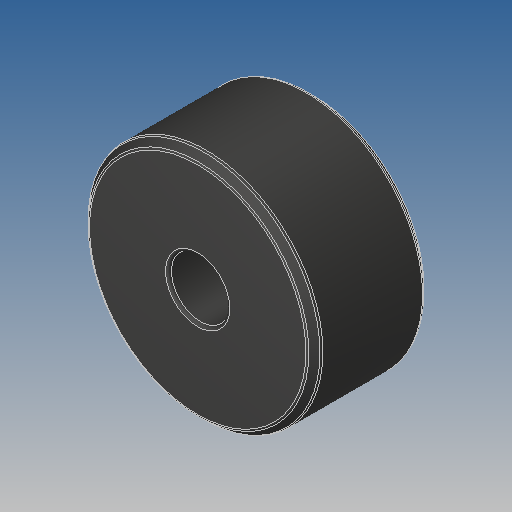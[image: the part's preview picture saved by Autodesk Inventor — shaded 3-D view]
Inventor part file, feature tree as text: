
AUTODESK INVENTOR PART (.ipt)
format: ipt  version: 2020 (Build 240168000, 168)  size: 142,848 bytes
history: mixed  units: mm
features: other x1, fillet x1, imported_body x1
ambient origin geometry x8: Origin, YZ Plane, XZ Plane, XY Plane, X Axis, Y Axis, Z Axis, Center Point
bodies: Body1 (imported_parasolid)
feature tree (3):
  other  "Твердое тело1"
  fillet  "Fillet1"  [1 undecoded]
  imported_body  NMx_Import_Brep_tag  [imported B-rep: ~12 faces, bbox_mm=[8.0, 0.0, 4.0]]
note: 1 required parameter value undecoded (feature->parameter linkage not recoverable at this tier; creation-order binding heuristic only, values carry confidence <= 0.55)
